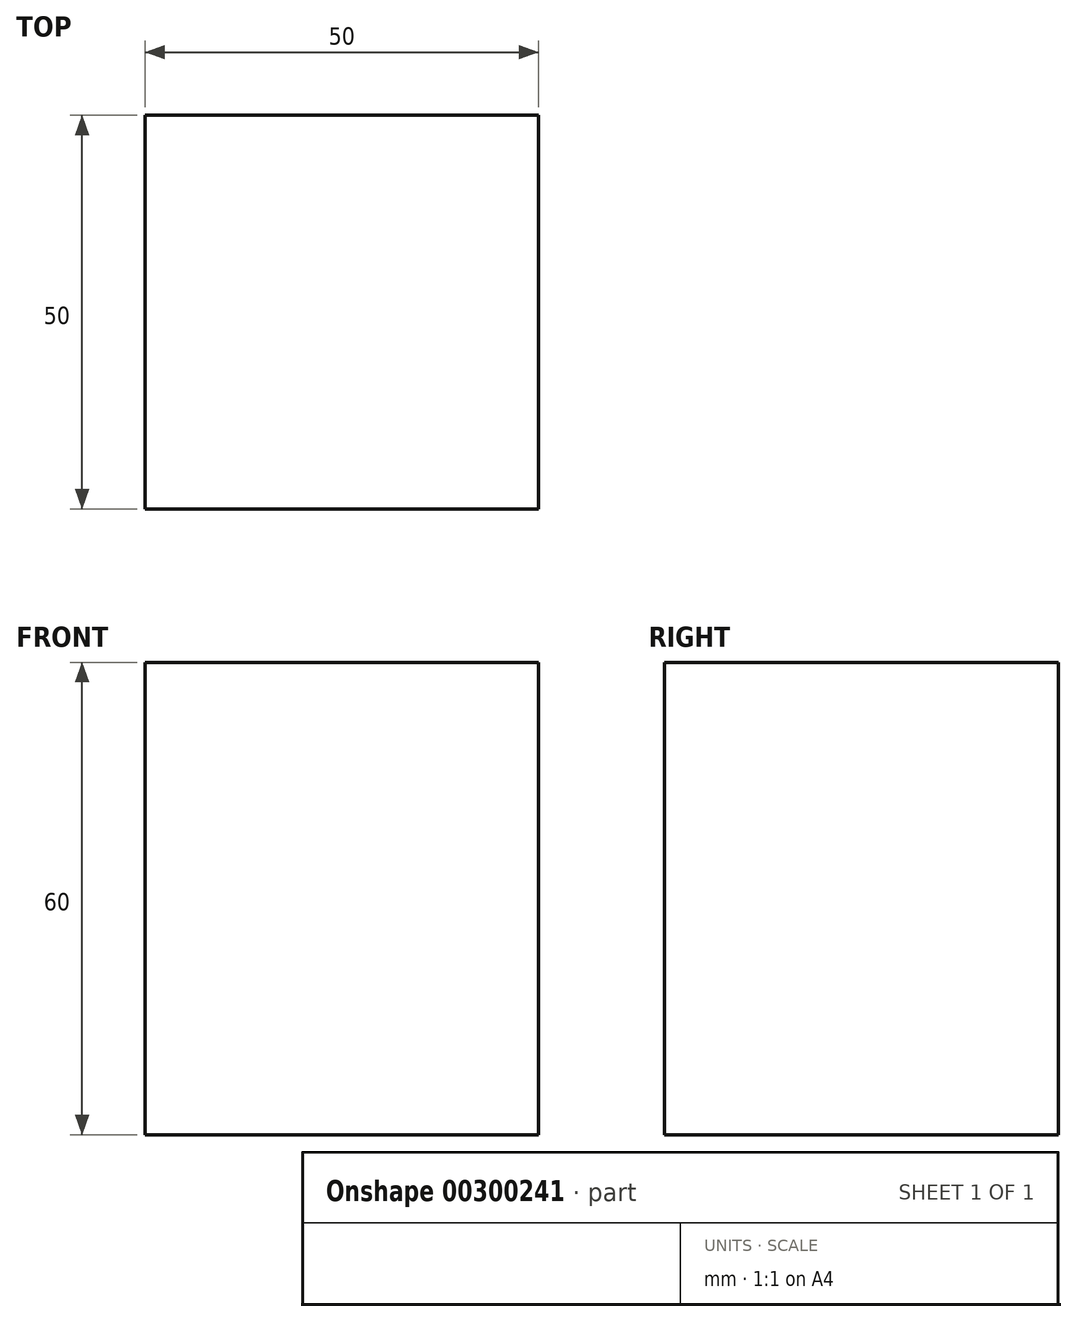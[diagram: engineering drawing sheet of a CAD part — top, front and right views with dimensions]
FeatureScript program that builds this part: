
annotation { "Feature Type Name" : "Feature", "Feature Type Description" : "" }
export const myFeature = defineFeature(function(context is Context, id is Id, definition is map)
    precondition{}
    {
        {
            var Q0;
            Q0=qCreatedBy(makeId("Front.planeOp"),FACE);
            var sketch = newSketch(context, id + "F0", { "sketchPlane" : qUnion([Q0])});
            skLineSegment(sketch, "E0.bottom", {"start": v(25, 30) * mm, "end": v(-25, 30) * mm});
            skLineSegment(sketch, "E0.top", {"start": v(25, -30) * mm, "end": v(-25, -30) * mm});
            skLineSegment(sketch, "E0.left", {"start": v(25, 30) * mm, "end": v(25, -30) * mm});
            skLineSegment(sketch, "E0.right", {"start": v(-25, 30) * mm, "end": v(-25, -30) * mm});
            skPoint(sketch, "E0.middle", {"position": v(0, 0) * mm});
            skSolve(sketch);
        }
        {
            var Q0;
            Q0=makeQuery(id+"F0.imprint","IMPRINT",FACE,{"disambiguationData":[TD([[makeQuery(id+"F0.imprint","IMPRINT",EDGE,{"derivedFrom":sQuery(id+"F0.wireOp",EDGE,"E0.bottom")}),1.0]])]});
            extrude(context, id + "F1", {"entities" : qUnion([Q0]), "depth" : 50 * mm});
        }
    });
